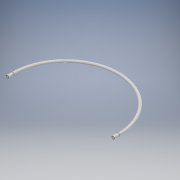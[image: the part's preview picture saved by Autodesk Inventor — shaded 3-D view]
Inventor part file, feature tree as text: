
AUTODESK INVENTOR PART (.ipt)
format: ipt  version: 2017 (Build 210142000, 142)  size: 111,616 bytes
history: native  units: mm
features: sketch x2, other x1, sweep x1
ambient origin geometry x8: Origin, YZ Plane, XZ Plane, XY Plane, X Axis, Y Axis, Z Axis, Center Point
bodies: Body1 (feature_tree)
feature tree (4):
  other  "Твердое тело1"
  sweep  "Сдвиг1"
  sketch  "Эскиз1"
  sketch  "Эскиз3"
